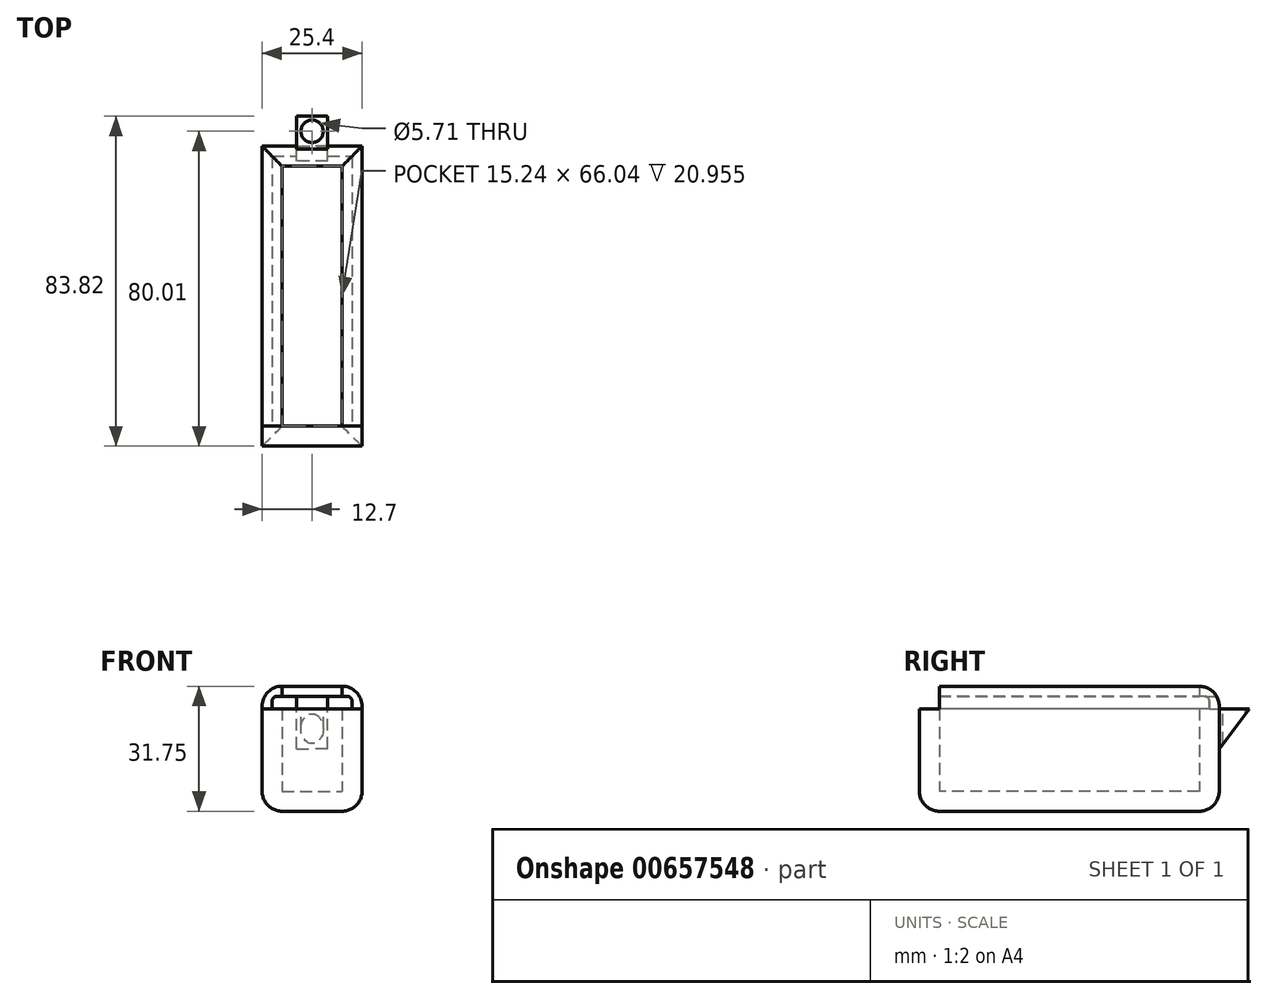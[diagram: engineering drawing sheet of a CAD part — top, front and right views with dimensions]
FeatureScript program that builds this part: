
annotation { "Feature Type Name" : "Feature", "Feature Type Description" : "" }
export const myFeature = defineFeature(function(context is Context, id is Id, definition is map)
    precondition{}
    {
        {
            var Q0;
            Q0=qCreatedBy(makeId("Top.planeOp"),FACE);
            var sketch = newSketch(context, id + "F0", { "sketchPlane" : qUnion([Q0])});
            skLineSegment(sketch, "E0.bottom", {"start": v(-12.7, 38.1) * mm, "end": v(12.7, 38.1) * mm});
            skLineSegment(sketch, "E0.top", {"start": v(-12.7, -38.1) * mm, "end": v(12.7, -38.1) * mm});
            skLineSegment(sketch, "E0.left", {"start": v(-12.7, 38.1) * mm, "end": v(-12.7, -38.1) * mm});
            skLineSegment(sketch, "E0.right", {"start": v(12.7, 38.1) * mm, "end": v(12.7, -38.1) * mm});
            skPoint(sketch, "E0.middle", {"position": v(0, 0) * mm});
            skSolve(sketch);
        }
        {
            var Q0;
            Q0 = qSketchRegion(id + "F0", true);
            extrude(context, id + "F1", {"entities" : qUnion([Q0]), "depth" : 31.75 * mm, "offsetDistance" : 25.4 * mm});
        }
        {
            var Q0;
            Q0=makeQuery(id+"F1.opExtrude","CAP_FACE",FACE,{"disambiguationData":[OSD([sQuery(id+"F0.wireOp",EDGE,"E0.bottom"),sQuery(id+"F0.wireOp",EDGE,"E0.top"),sQuery(id+"F0.wireOp",EDGE,"E0.left"),sQuery(id+"F0.wireOp",EDGE,"E0.right")])],"isStart":false});
            shell(context, id + "F2", {"entities" : qUnion([Q0]), "thickness" : 5.08 * mm});
        }
        {
            var Q0;
            Q0=makeQuery(id+"F2.opShell","OFFSET_FACE",FACE,{"disambiguationData":[OSD([sQuery(id+"F0.wireOp",EDGE,"E0.top")])]});
            var sketch = newSketch(context, id + "F3", { "sketchPlane" : qUnion([Q0])});
            skLineSegment(sketch, "E1.bottom", {"start": v(-7.62, 31.75) * mm, "end": v(7.62, 31.75) * mm});
            skLineSegment(sketch, "E1.top", {"start": v(-7.62, 26.04) * mm, "end": v(7.62, 26.04) * mm});
            skLineSegment(sketch, "E1.left", {"start": v(-7.62, 31.75) * mm, "end": v(-7.62, 26.04) * mm});
            skLineSegment(sketch, "E1.right", {"start": v(7.62, 31.75) * mm, "end": v(7.62, 26.04) * mm});
            skSolve(sketch);
        }
        {
            var Q0;
            Q0 = qSketchRegion(id + "F3", true);
            extrude(context, id + "F4", {"entities" : qUnion([Q0]), "operationType" : NewBodyOperationType.REMOVE, "oppositeDirection" : true, "depth" : 25.4 * mm, "offsetDistance" : 25.4 * mm});
        }
        {
            var Q0;
            Q0=makeQuery(id+"F1.opExtrude","SWEPT_FACE",FACE,{"disambiguationData":[OSD([sQuery(id+"F0.wireOp",EDGE,"E0.top")])]});
            var sketch = newSketch(context, id + "F5", { "sketchPlane" : qUnion([Q0])});
            skLineSegment(sketch, "E2", {"start": v(-7.62, 26.04) * mm, "end": v(-10.16, 26.04) * mm});
            skLineSegment(sketch, "E3", {"start": v(-10.16, 26.04) * mm, "end": v(-10.16, 29.21) * mm});
            skLineSegment(sketch, "E4", {"start": v(-10.16, 29.21) * mm, "end": v(10.16, 29.21) * mm});
            skLineSegment(sketch, "E5", {"start": v(10.16, 29.21) * mm, "end": v(10.16, 26.04) * mm});
            skLineSegment(sketch, "E6", {"start": v(10.16, 26.04) * mm, "end": v(-7.62, 26.04) * mm});
            skSolve(sketch);
        }
        {
            var Q0;
            Q0 = qSketchRegion(id + "F5", true);
            extrude(context, id + "F6", {"entities" : qUnion([Q0]), "operationType" : NewBodyOperationType.REMOVE, "oppositeDirection" : true, "depth" : 73.66 * mm, "offsetDistance" : 25.4 * mm});
        }
        {
            var Q0;
            Q0=makeQuery(id+"F6.boolean.opBoolean","COPY",EDGE,{"derivedFrom":makeQuery(id+"F6.opExtrude","SWEPT_EDGE",EDGE,{"disambiguationData":[OSD([sQuery(id+"F5.wireOp",EDGE,"E3"),sQuery(id+"F5.wireOp",EDGE,"E4")])]})});
            var Q1;
            Q1=makeQuery(id+"F6.boolean.opBoolean","COPY",EDGE,{"derivedFrom":makeQuery(id+"F6.opExtrude","CAP_EDGE",EDGE,{"disambiguationData":[OSD([sQuery(id+"F5.wireOp",EDGE,"E4")])],"isStart":false})});
            var Q2;
            Q2=makeQuery(id+"F6.boolean.opBoolean","COPY",EDGE,{"derivedFrom":makeQuery(id+"F6.opExtrude","SWEPT_EDGE",EDGE,{"disambiguationData":[OSD([sQuery(id+"F5.wireOp",EDGE,"E4"),sQuery(id+"F5.wireOp",EDGE,"E5")])]})});
            fillet(context, id + "F7", {"entities" : qUnion([Q0, Q1, Q2]), "radius" : 1.27 * mm, "tangentPropagation" : true, "allowEdgeOverflow" : false});
        }
        {
            var Q0;
            Q0=qCreatedBy(makeId("Right.planeOp"),FACE);
            var sketch = newSketch(context, id + "F8", { "sketchPlane" : qUnion([Q0])});
            skLineSegment(sketch, "E7", {"start": v(38.1, 31.75) * mm, "end": v(38.1, 26.03) * mm});
            skLineSegment(sketch, "E8", {"start": v(38.1, 15.87) * mm, "end": v(38.1, 26.03) * mm});
            skLineSegment(sketch, "E9", {"start": v(38.1, 26.03) * mm, "end": v(45.72, 26.03) * mm});
            skLineSegment(sketch, "E10", {"start": v(45.72, 26.03) * mm, "end": v(38.1, 15.87) * mm});
            skSolve(sketch);
        }
        {
            var Q0;
            Q0 = qSketchRegion(id + "F8", true);
            extrude(context, id + "F9", {"entities" : qUnion([Q0]), "operationType" : NewBodyOperationType.ADD, "depth" : 3.94 * mm, "offsetDistance" : 25.4 * mm});
        }
        {
            var Q0;
            Q0 = qSketchRegion(id + "F8", true);
            extrude(context, id + "F10", {"entities" : qUnion([Q0]), "operationType" : NewBodyOperationType.ADD, "oppositeDirection" : true, "depth" : 3.94 * mm, "offsetDistance" : 25.4 * mm});
        }
        {
            var Q0;
            Q0=makeQuery(id+"F1.opExtrude","SWEPT_FACE",FACE,{"disambiguationData":[OSD([sQuery(id+"F0.wireOp",EDGE,"E0.top")])]});
            var sketch = newSketch(context, id + "F11", { "sketchPlane" : qUnion([Q0])});
            skLineSegment(sketch, "E11", {"start": v(-10.16, 26.04) * mm, "end": v(10.16, 26.04) * mm});
            skLineSegment(sketch, "E12", {"start": v(10.16, 26.04) * mm, "end": v(10.16, 31.75) * mm});
            skLineSegment(sketch, "E13", {"start": v(10.16, 31.75) * mm, "end": v(-10.16, 31.75) * mm});
            skLineSegment(sketch, "E14", {"start": v(-10.16, 31.75) * mm, "end": v(-10.16, 26.04) * mm});
            skSolve(sketch);
        }
        {
            var Q0;
            Q0 = qSketchRegion(id + "F11", true);
            extrude(context, id + "F12", {"entities" : qUnion([Q0]), "operationType" : NewBodyOperationType.REMOVE, "oppositeDirection" : true, "depth" : 5.08 * mm, "offsetDistance" : 25.4 * mm});
        }
        {
            var Q0;
            {var subQ0=sQuery(id+"F8.wireOp",EDGE,"E9");Q0=makeQuery(id+"F10.boolean.opBoolean","MERGE",FACE,{"derivedFrom":[makeQuery(id+"F9.opExtrude","SWEPT_FACE",FACE,{"disambiguationData":[OSD([subQ0])]}),makeQuery(id+"F10.opExtrude","SWEPT_FACE",FACE,{"disambiguationData":[OSD([subQ0])]})]});}
            var sketch = newSketch(context, id + "F13", { "sketchPlane" : qUnion([Q0])});
            skCircle(sketch, "E15", {"center": v(0, 41.9) * mm, "radius": 2.86 * mm});
            skPoint(sketch, "E15.centerSnap0", {"position": v(-3.94, 41.9) * mm});
            skPoint(sketch, "E15.centerSnap1", {"position": v(0, 45.72) * mm});
            skSolve(sketch);
        }
        {
            var Q0;
            Q0 = qSketchRegion(id + "F13", true);
            extrude(context, id + "F14", {"entities" : qUnion([Q0]), "operationType" : NewBodyOperationType.REMOVE, "oppositeDirection" : true, "depth" : 25.4 * mm, "offsetDistance" : 25.4 * mm});
        }
        {
            var Q0;
            Q0=makeQuery(id+"F1.opExtrude","SWEPT_FACE",FACE,{"disambiguationData":[OSD([sQuery(id+"F0.wireOp",EDGE,"E0.bottom")])]});
            var sketch = newSketch(context, id + "F15", { "sketchPlane" : qUnion([Q0])});
            skLineSegment(sketch, "E16.bottom", {"start": v(-3.94, 26.03) * mm, "end": v(3.94, 26.03) * mm});
            skLineSegment(sketch, "E16.top", {"start": v(-3.94, 29.2) * mm, "end": v(3.94, 29.2) * mm});
            skLineSegment(sketch, "E16.left", {"start": v(-3.94, 26.03) * mm, "end": v(-3.94, 29.2) * mm});
            skLineSegment(sketch, "E16.right", {"start": v(3.94, 26.03) * mm, "end": v(3.94, 29.2) * mm});
            skSolve(sketch);
        }
        {
            var Q0;
            Q0 = qSketchRegion(id + "F15", true);
            extrude(context, id + "F16", {"entities" : qUnion([Q0]), "operationType" : NewBodyOperationType.REMOVE, "oppositeDirection" : true, "depth" : 25.4 * mm, "offsetDistance" : 25.4 * mm});
        }
        {
            var Q0;
            Q0=makeQuery(id+"F12.boolean.opBoolean","MERGE",FACE,{"derivedFrom":[makeQuery(id+"F6.boolean.opBoolean","COPY",FACE,{"derivedFrom":makeQuery(id+"F6.opExtrude","SWEPT_FACE",FACE,{"disambiguationData":[OSD([sQuery(id+"F5.wireOp",EDGE,"E3")])]})}),makeQuery(id+"F12.opExtrude","SWEPT_FACE",FACE,{"disambiguationData":[OSD([sQuery(id+"F11.wireOp",EDGE,"E14")])]})]});
            var sketch = newSketch(context, id + "F17", { "sketchPlane" : qUnion([Q0])});
            skLineSegment(sketch, "E17.bottom", {"start": v(-33.02, 31.75) * mm, "end": v(-38.1, 31.75) * mm});
            skLineSegment(sketch, "E17.top", {"start": v(-33.02, 26.04) * mm, "end": v(-38.1, 26.04) * mm});
            skLineSegment(sketch, "E17.left", {"start": v(-33.02, 31.75) * mm, "end": v(-33.02, 26.04) * mm});
            skLineSegment(sketch, "E17.right", {"start": v(-38.1, 31.75) * mm, "end": v(-38.1, 26.04) * mm});
            skSolve(sketch);
        }
        {
            var Q0;
            Q0 = qSketchRegion(id + "F17", true);
            extrude(context, id + "F18", {"entities" : qUnion([Q0]), "operationType" : NewBodyOperationType.REMOVE, "oppositeDirection" : true, "depth" : 25.4 * mm, "offsetDistance" : 25.4 * mm});
        }
        {
            var Q0;
            Q0 = qSketchRegion(id + "F17", true);
            extrude(context, id + "F19", {"entities" : qUnion([Q0]), "operationType" : NewBodyOperationType.REMOVE, "depth" : 50.8 * mm, "offsetDistance" : 25.4 * mm});
        }
        {
            var Q0;
            Q0=makeQuery(id+"F1.opExtrude","CAP_FACE",FACE,{"disambiguationData":[OSD([sQuery(id+"F0.wireOp",EDGE,"E0.bottom"),sQuery(id+"F0.wireOp",EDGE,"E0.top"),sQuery(id+"F0.wireOp",EDGE,"E0.left"),sQuery(id+"F0.wireOp",EDGE,"E0.right")])],"isStart":true});
            var Q1;
            Q1=makeQuery(id+"F1.opExtrude","CAP_EDGE",EDGE,{"disambiguationData":[OSD([sQuery(id+"F0.wireOp",EDGE,"E0.left")])],"isStart":false});
            var Q2;
            Q2=makeQuery(id+"F1.opExtrude","CAP_EDGE",EDGE,{"disambiguationData":[OSD([sQuery(id+"F0.wireOp",EDGE,"E0.bottom")])],"isStart":false});
            var Q3;
            Q3=makeQuery(id+"F1.opExtrude","CAP_EDGE",EDGE,{"disambiguationData":[OSD([sQuery(id+"F0.wireOp",EDGE,"E0.right")])],"isStart":false});
            fillet(context, id + "F20", {"entities" : qUnion([Q0, Q1, Q2, Q3]), "radius" : 5.08 * mm, "tangentPropagation" : true, "allowEdgeOverflow" : false});
        }
    });
